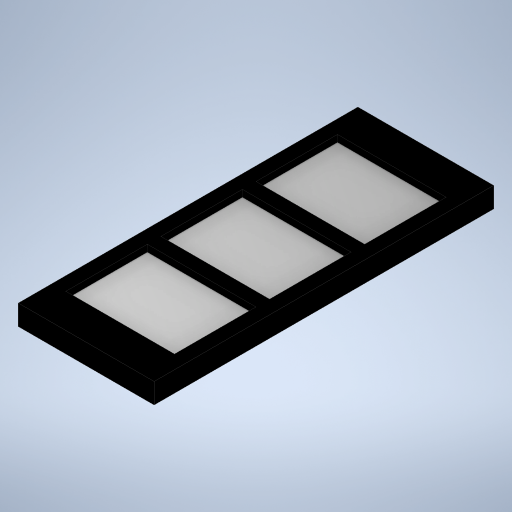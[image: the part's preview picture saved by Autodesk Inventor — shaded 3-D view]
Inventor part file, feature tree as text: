
AUTODESK INVENTOR PART (.ipt)
format: ipt  version: 2024 (Build 280153000, 153)  size: 257,536 bytes
history: native  units: mm
features: extrude x2, sketch x1
ambient origin geometry x8: Origin, YZ Plane, XZ Plane, XY Plane, X Axis, Y Axis, Z Axis, Center Point
bodies: Solid1 (feature_tree)
feature tree (3):
  extrude  "Extrusion1"  Depth=50.0mm
  extrude  "Extrusion3"  Depth=3.0mm TaperAngle=0.0deg
  sketch  "Sketch3"  dims[d0=20.0mm d1=50.0mm d2=3.0mm d3=0.0mm d14=2.0mm d15=2.0mm d16=5.0mm d17=5.0mm d20=1.0mm d21=0.0mm d22=12.0mm d23=12.0mm d24=12.0mm d25=2.0mm]
